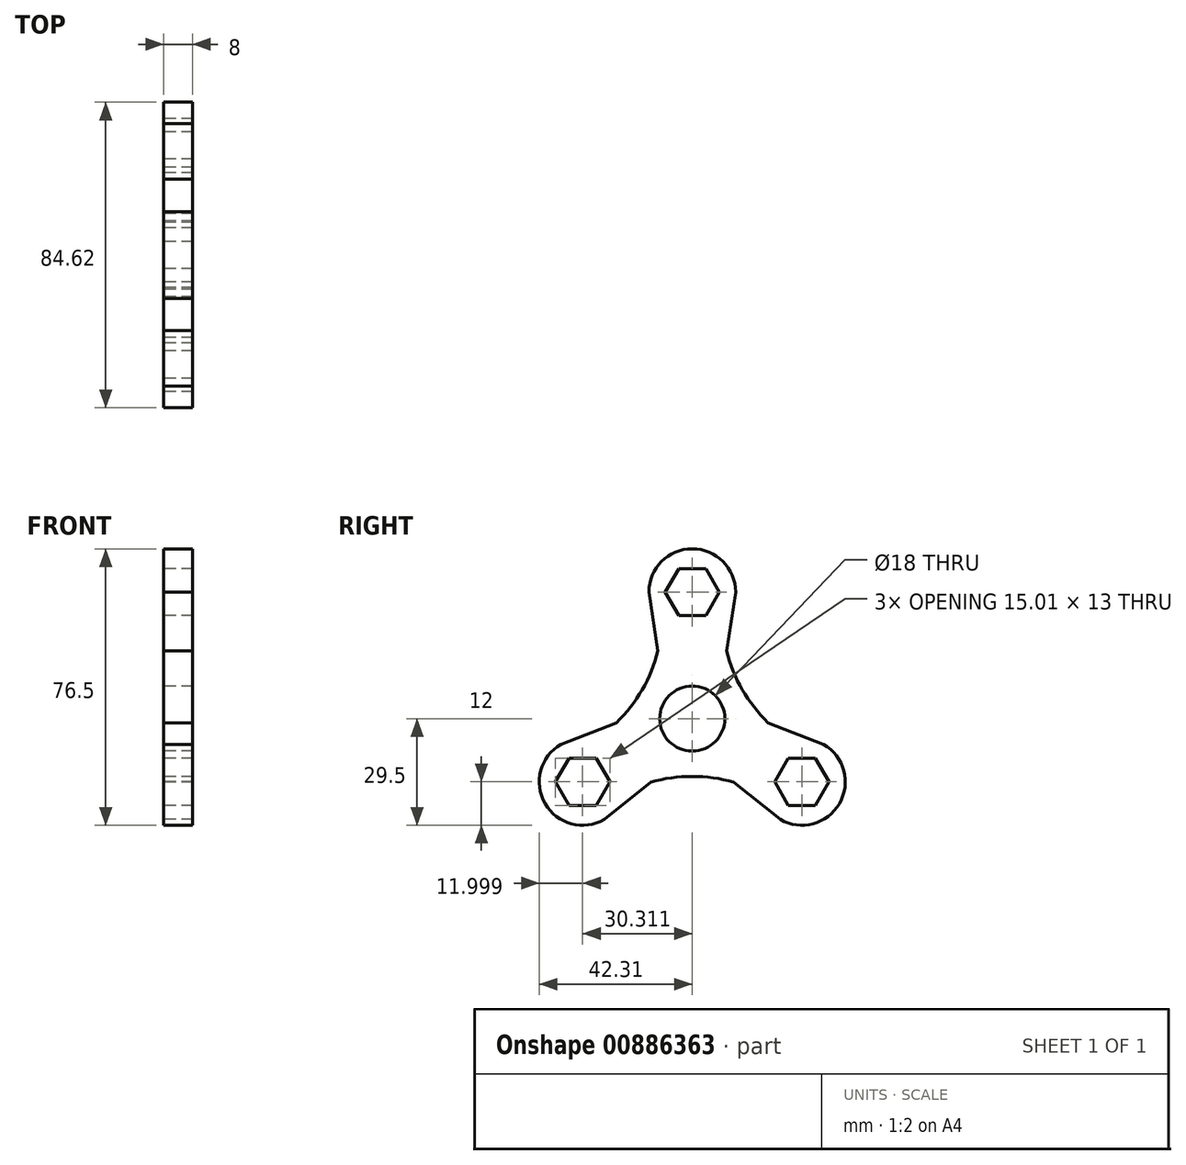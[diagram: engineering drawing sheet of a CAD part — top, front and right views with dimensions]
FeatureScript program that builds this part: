
annotation { "Feature Type Name" : "Feature", "Feature Type Description" : "" }
export const myFeature = defineFeature(function(context is Context, id is Id, definition is map)
    precondition{}
    {
        {
            var Q0;
            Q0=qCreatedBy(makeId("Right.planeOp"),FACE);
            var sketch = newSketch(context, id + "F0", { "sketchPlane" : qUnion([Q0])});
            skLineSegment(sketch, "E0", {"start": v(0, 0) * mm, "end": v(-30.7, -17.72) * mm, "construction": true});
            skLineSegment(sketch, "E1", {"start": v(0, 0) * mm, "end": v(30.47, -17.6) * mm, "construction": true});
            skCircle(sketch, "E2", {"center": v(0, 0) * mm, "radius": 9 * mm});
            skCircle(sketch, "E3.cCircle", {"center": v(0, 35) * mm, "radius": 6.5 * mm, "construction": true});
            skLineSegment(sketch, "E3.0", {"start": v(3.75, 28.5) * mm, "end": v(-3.75, 28.5) * mm});
            skLineSegment(sketch, "E3.1", {"start": v(-3.75, 28.5) * mm, "end": v(-7.5, 35) * mm});
            skLineSegment(sketch, "E3.2", {"start": v(-7.5, 35) * mm, "end": v(-3.75, 41.5) * mm});
            skLineSegment(sketch, "E3.3", {"start": v(-3.75, 41.5) * mm, "end": v(3.75, 41.5) * mm});
            skLineSegment(sketch, "E3.4", {"start": v(3.75, 41.5) * mm, "end": v(7.5, 35) * mm});
            skLineSegment(sketch, "E3.5", {"start": v(7.5, 35) * mm, "end": v(3.75, 28.5) * mm});
            skPoint(sketch, "E3.0.midPoint", {"position": v(0, 28.5) * mm});
            skArc(sketch, "E4", {"start": v(12, 35) * mm, "mid": v(0, 47) * mm, "end": v(-12, 35) * mm});
            skCircle(sketch, "E5", {"center": v(0, 0) * mm, "radius": 16.24 * mm, "construction": true});
            skCircle(sketch, "E6", {"center": v(0, 0) * mm, "radius": 20.97 * mm, "construction": true});
            skLineSegment(sketch, "E7", {"start": v(12, 35) * mm, "end": v(9.48, 18.7) * mm});
            skLineSegment(sketch, "E8.MirrorCS", {"start": v(-12, 35) * mm, "end": v(-9.48, 18.7) * mm});
            skArc(sketch, "E9.1.0", {"start": v(-36.31, -7.1) * mm, "mid": v(-40.7, -23.5) * mm, "end": v(-24.31, -27.9) * mm});
            skLineSegment(sketch, "E9.1.1", {"start": v(-36.31, -7.1) * mm, "end": v(-20.94, -1.14) * mm});
            skLineSegment(sketch, "E9.1.2", {"start": v(-24.31, -27.9) * mm, "end": v(-11.46, -17.57) * mm});
            skCircle(sketch, "E9.1.3", {"center": v(-30.31, -17.5) * mm, "radius": 6.5 * mm, "construction": true});
            skPoint(sketch, "E9.1.4", {"position": v(-24.68, -14.25) * mm});
            skLineSegment(sketch, "E9.1.5", {"start": v(-22.8, -17.5) * mm, "end": v(-26.56, -24) * mm});
            skLineSegment(sketch, "E9.1.6", {"start": v(-26.56, -11) * mm, "end": v(-22.8, -17.5) * mm});
            skLineSegment(sketch, "E9.1.7", {"start": v(-34.06, -11) * mm, "end": v(-26.56, -11) * mm});
            skLineSegment(sketch, "E9.1.8", {"start": v(-37.82, -17.5) * mm, "end": v(-34.06, -11) * mm});
            skLineSegment(sketch, "E9.1.9", {"start": v(-34.06, -24) * mm, "end": v(-37.82, -17.5) * mm});
            skLineSegment(sketch, "E9.1.10", {"start": v(-26.56, -24) * mm, "end": v(-34.06, -24) * mm});
            skArc(sketch, "E9.2.0", {"start": v(24.31, -27.9) * mm, "mid": v(40.7, -23.5) * mm, "end": v(36.31, -7.1) * mm});
            skLineSegment(sketch, "E9.2.1", {"start": v(24.31, -27.9) * mm, "end": v(11.46, -17.57) * mm});
            skLineSegment(sketch, "E9.2.2", {"start": v(36.31, -7.1) * mm, "end": v(20.94, -1.14) * mm});
            skCircle(sketch, "E9.2.3", {"center": v(30.31, -17.5) * mm, "radius": 6.5 * mm, "construction": true});
            skPoint(sketch, "E9.2.4", {"position": v(24.68, -14.25) * mm});
            skLineSegment(sketch, "E9.2.5", {"start": v(26.56, -11) * mm, "end": v(34.06, -11) * mm});
            skLineSegment(sketch, "E9.2.6", {"start": v(22.8, -17.5) * mm, "end": v(26.56, -11) * mm});
            skLineSegment(sketch, "E9.2.7", {"start": v(26.56, -24) * mm, "end": v(22.8, -17.5) * mm});
            skLineSegment(sketch, "E9.2.8", {"start": v(34.06, -24) * mm, "end": v(26.56, -24) * mm});
            skLineSegment(sketch, "E9.2.9", {"start": v(37.82, -17.5) * mm, "end": v(34.06, -24) * mm});
            skLineSegment(sketch, "E9.2.10", {"start": v(34.06, -11) * mm, "end": v(37.82, -17.5) * mm});
            skArc(sketch, "E10", {"start": v(9.48, 18.7) * mm, "mid": v(13.85, 8) * mm, "end": v(20.94, -1.14) * mm});
            skArc(sketch, "E11.1.0", {"start": v(-20.94, -1.14) * mm, "mid": v(-13.85, 8) * mm, "end": v(-9.48, 18.7) * mm});
            skArc(sketch, "E11.2.0", {"start": v(11.46, -17.57) * mm, "mid": v(0, -16) * mm, "end": v(-11.46, -17.57) * mm});
            skSolve(sketch);
        }
        {
            var Q0;
            Q0 = qSketchRegion(id + "F0", true);
            extrude(context, id + "F1", {"entities" : qUnion([Q0]), "depth" : 8 * mm, "offsetDistance" : 25 * mm});
        }
    });
